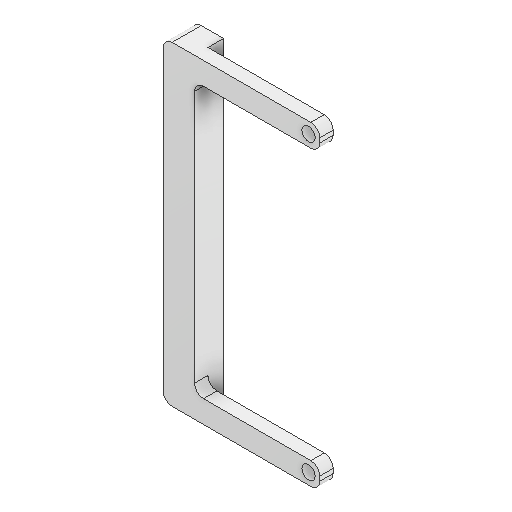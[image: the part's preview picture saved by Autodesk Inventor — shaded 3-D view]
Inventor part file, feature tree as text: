
AUTODESK INVENTOR PART (.ipt)
format: ipt  version: 2025.2 (Build 292293000, 293)  size: 136,192 bytes
history: native  units: mm
features: sketch x3, extrude x2, mirror x1, hole x1, fillet x1
ambient origin geometry x8: Origin, YZ Plane, XZ Plane, XY Plane, X Axis, Y Axis, Z Axis, Center Point
bodies: Solid1 (feature_tree)
feature tree (8):
  extrude  "Extrusion1"  Depth=5.0mm
  mirror  "Mirror1"
  extrude  "Extrusion2"  Depth=35.0mm
  hole  "Hole1"  [1 undecoded]
  fillet  "Fillet1"  Radius=65.5mm
  sketch  "Sketch1"  dims[d0=7.0mm d2=5.0mm]
  sketch  "Sketch2"  dims[d3=35.0mm d4=32.75mm]
  sketch  "Sketch3"  dims[d5=3.0mm d6=0.0mm d7=3.5mm d8=0.0mm d9=3.0mm d10=6.0mm d11=4.0mm d12=2.0mm d13=90.0deg d14=8.0mm d15=20.594885mm d16=65.5mm d17=2.0mm d18=2.5mm]
note: 1 required parameter value undecoded (feature->parameter linkage not recoverable at this tier; creation-order binding heuristic only, values carry confidence <= 0.55)
